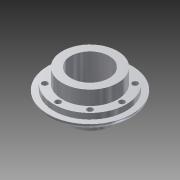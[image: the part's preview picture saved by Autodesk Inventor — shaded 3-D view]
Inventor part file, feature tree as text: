
AUTODESK INVENTOR PART (.ipt)
format: ipt  version: 2015 (Build 190159000, 159)  size: 155,136 bytes
history: native  units: mm
features: sketch x4, extrude x4, fillet x1, hole x1, pattern_circular x1, projected_geometry x1
ambient origin geometry x8: Origin, YZ Plane, XZ Plane, XY Plane, X Axis, Y Axis, Z Axis, Center Point
bodies: Solid1 (feature_tree)
feature tree (12):
  sketch  "Sketch1"  dims[d0=15.5mm d1=2.0mm]
  extrude  "Extrusion1"  Depth=2.0mm
  extrude  "Extrusion2"  Depth=5.0mm TaperAngle=0.0deg
  fillet  "Fillet1"  Radius=5.0mm
  extrude  "Extrusion3"  Depth=2.0mm
  extrude  "Extrusion4"  Depth=2.0mm
  hole  "Hole1"  [1 undecoded]
  pattern_circular  "Circular Pattern1"  [2 undecoded]
  sketch  "Sketch2"  dims[d2=1.0mm d3=5.0mm d4=0.0mm d5=5.0mm]
  sketch  "Sketch3"  dims[d6=2.0mm d7=0.0mm d8=2.0mm]
  sketch  "Sketch4"  dims[d9=25.5mm d10=13.5mm d11=2.0mm d12=0.0mm d13=3.0mm d14=5.0mm d15=0.0mm d17=2.0mm d18=6.0mm d19=4.0mm d20=2.0mm d21=90.0deg d22=3.0mm d23=20.594885mm d24=80.0mm d25=360.0deg d27=25.5mm]
  projected_geometry  "Projected Loop1"
note: 3 required parameter values undecoded (feature->parameter linkage not recoverable at this tier; creation-order binding heuristic only, values carry confidence <= 0.55)
